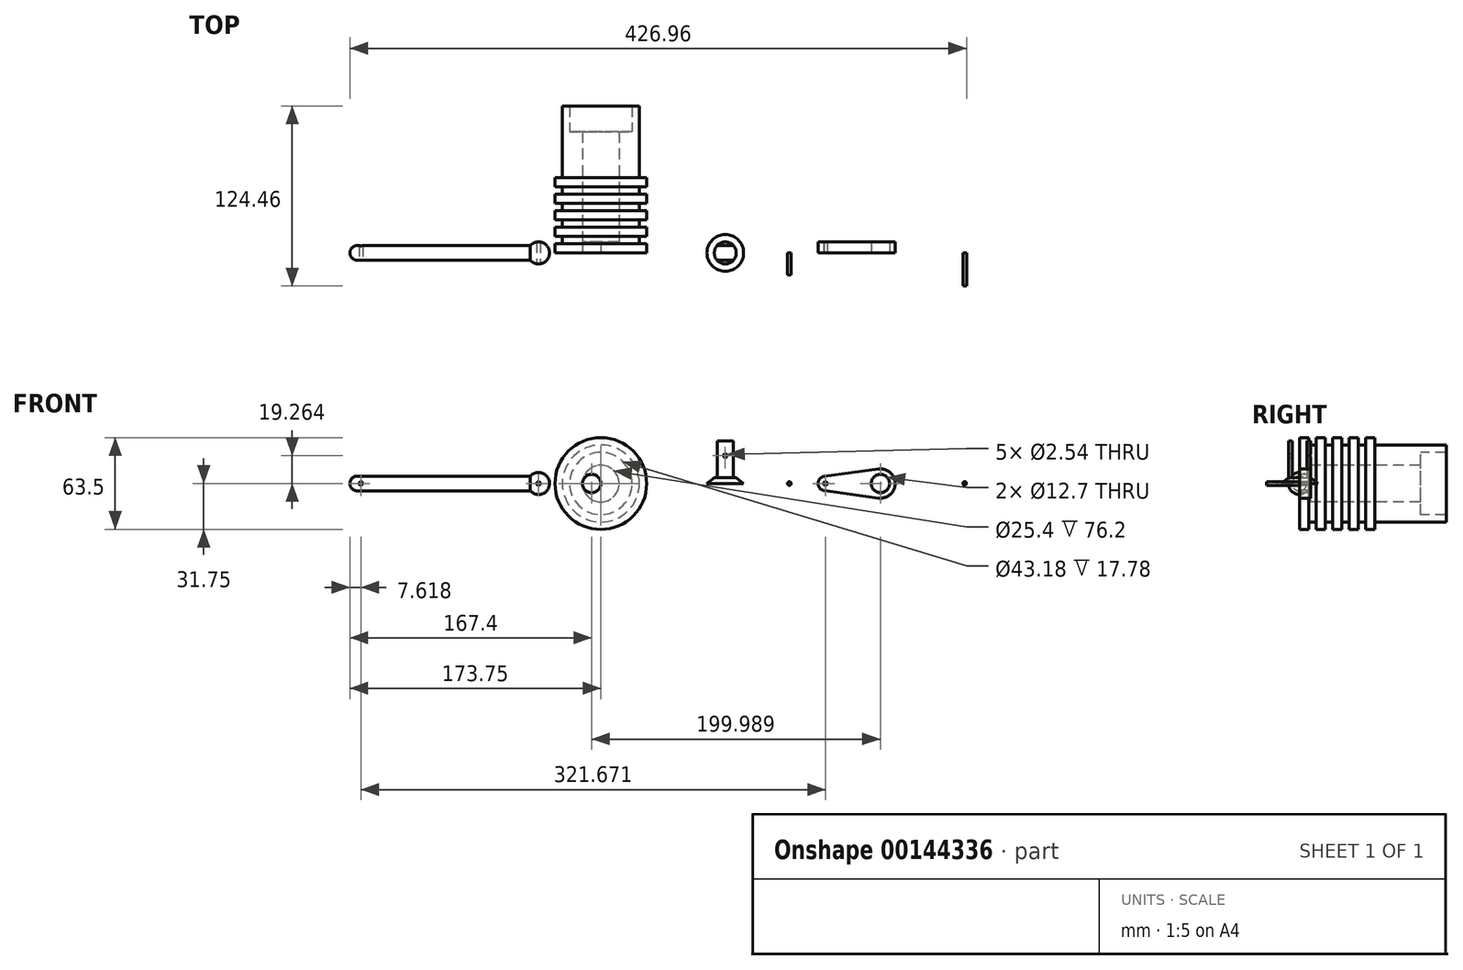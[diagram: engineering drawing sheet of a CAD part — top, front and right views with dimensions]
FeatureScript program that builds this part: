
annotation { "Feature Type Name" : "Feature", "Feature Type Description" : "" }
export const myFeature = defineFeature(function(context is Context, id is Id, definition is map)
    precondition{}
    {
        {
            var Q0;
            Q0=qCreatedBy(makeId("Top.planeOp"),FACE);
            var sketch = newSketch(context, id + "F0", { "sketchPlane" : qUnion([Q0])});
            skLineSegment(sketch, "E0", {"start": v(-31.75, 0) * mm, "end": v(-31.75, 6.35) * mm});
            skLineSegment(sketch, "E1", {"start": v(-31.75, 6.35) * mm, "end": v(-26.67, 6.35) * mm});
            skLineSegment(sketch, "E2", {"start": v(-26.67, 6.35) * mm, "end": v(-26.67, 11.43) * mm});
            skLineSegment(sketch, "E3", {"start": v(-26.67, 11.43) * mm, "end": v(-31.75, 11.43) * mm});
            skLineSegment(sketch, "E4", {"start": v(-31.75, 11.43) * mm, "end": v(-31.75, 17.78) * mm});
            skLineSegment(sketch, "E5", {"start": v(-31.75, 17.78) * mm, "end": v(-26.67, 17.78) * mm});
            skLineSegment(sketch, "E6", {"start": v(-26.67, 17.78) * mm, "end": v(-26.67, 22.86) * mm});
            skLineSegment(sketch, "E7", {"start": v(-26.67, 22.86) * mm, "end": v(-31.75, 22.86) * mm});
            skLineSegment(sketch, "E8", {"start": v(-31.75, 22.86) * mm, "end": v(-31.75, 29.21) * mm});
            skLineSegment(sketch, "E9", {"start": v(-31.75, 29.21) * mm, "end": v(-26.67, 29.21) * mm});
            skLineSegment(sketch, "E10", {"start": v(-26.67, 29.21) * mm, "end": v(-26.67, 34.3) * mm});
            skLineSegment(sketch, "E11", {"start": v(-26.67, 34.3) * mm, "end": v(-31.75, 34.3) * mm});
            skLineSegment(sketch, "E12", {"start": v(-31.75, 34.3) * mm, "end": v(-31.75, 40.64) * mm});
            skLineSegment(sketch, "E13", {"start": v(-31.75, 40.64) * mm, "end": v(-26.67, 40.64) * mm});
            skLineSegment(sketch, "E14", {"start": v(-26.67, 40.64) * mm, "end": v(-26.67, 45.72) * mm});
            skLineSegment(sketch, "E15", {"start": v(-26.67, 45.72) * mm, "end": v(-31.75, 45.72) * mm});
            skLineSegment(sketch, "E16", {"start": v(-31.75, 45.72) * mm, "end": v(-31.75, 52.07) * mm});
            skLineSegment(sketch, "E17", {"start": v(-31.75, 52.07) * mm, "end": v(-26.67, 52.07) * mm});
            skLineSegment(sketch, "E18", {"start": v(-26.67, 52.07) * mm, "end": v(-26.67, 101.6) * mm});
            skLineSegment(sketch, "E19", {"start": v(-26.67, 101.6) * mm, "end": v(-21.6, 101.6) * mm});
            skLineSegment(sketch, "E20", {"start": v(-21.6, 101.6) * mm, "end": v(-21.6, 83.82) * mm});
            skLineSegment(sketch, "E21", {"start": v(-21.6, 83.82) * mm, "end": v(-12.7, 83.82) * mm});
            skLineSegment(sketch, "E22", {"start": v(-1.27, 7.62) * mm, "end": v(-12.7, 7.62) * mm});
            skLineSegment(sketch, "E23", {"start": v(-12.7, 7.62) * mm, "end": v(-12.7, 83.82) * mm});
            skLineSegment(sketch, "E24", {"start": v(-31.75, 0) * mm, "end": v(-1.27, 0) * mm});
            skLineSegment(sketch, "E25", {"start": v(-1.27, 0) * mm, "end": v(-1.27, 7.62) * mm});
            skLineSegment(sketch, "E26", {"start": v(0, 0) * mm, "end": v(0, 138.75) * mm, "construction": true});
            skSolve(sketch);
        }
        {
            var Q0;
            Q0 = qSketchRegion(id + "F0", true);
            var Q1;
            Q1=sQuery(id+"F0.wireOp",EDGE,"E26");
            revolve(context, id + "F1", {"entities" : qUnion([Q0]), "axis" : qUnion([Q1]), "revolveType" : RevolveType.FULL});
        }
        {
            var Q0;
            Q0=makeQuery(id+"F1.opRevolve","SWEPT_FACE",FACE,{"disambiguationData":[OSD([sQuery(id+"F0.wireOp",EDGE,"E24")])]});
            var sketch = newSketch(context, id + "F2", { "sketchPlane" : qUnion([Q0])});
            skCircle(sketch, "E27.0", {"center": v(0, 0) * mm, "radius": 1.27 * mm});
            skSolve(sketch);
        }
        {
            var Q0;
            Q0 = qSketchRegion(id + "F2", true);
            extrude(context, id + "F3", {"entities" : qUnion([Q0]), "operationType" : NewBodyOperationType.ADD, "oppositeDirection" : true, "depth" : 7.62 * mm});
        }
        {
            var Q0;
            Q0=qCreatedBy(makeId("Front.planeOp"),FACE);
            var sketch = newSketch(context, id + "F4", { "sketchPlane" : qUnion([Q0])});
            skLineSegment(sketch, "E28", {"start": v(86.19, 0) * mm, "end": v(86.19, 29.98) * mm, "construction": true});
            skLineSegment(sketch, "E29", {"start": v(73.49, 0) * mm, "end": v(78.57, 4.02) * mm});
            skLineSegment(sketch, "E30", {"start": v(78.57, 4.02) * mm, "end": v(86.19, 4.02) * mm});
            skLineSegment(sketch, "E31", {"start": v(86.19, 4.02) * mm, "end": v(86.19, 0) * mm});
            skLineSegment(sketch, "E32", {"start": v(73.49, 0) * mm, "end": v(86.19, 0) * mm});
            skSolve(sketch);
        }
        {
            var Q0;
            Q0 = qSketchRegion(id + "F4", true);
            var Q1;
            Q1=sQuery(id+"F4.wireOp",EDGE,"E28");
            revolve(context, id + "F5", {"entities" : qUnion([Q0]), "axis" : qUnion([Q1]), "revolveType" : RevolveType.FULL});
        }
        {
            var Q0;
            Q0=makeQuery(id+"F5.opRevolve","SWEPT_FACE",FACE,{"disambiguationData":[OSD([sQuery(id+"F4.wireOp",EDGE,"E30")])]});
            var sketch = newSketch(context, id + "F6", { "sketchPlane" : qUnion([Q0])});
            skLineSegment(sketch, "E33", {"start": v(80.5, 5.08) * mm, "end": v(91.87, 5.08) * mm});
            skLineSegment(sketch, "E34", {"start": v(80.5, -5.08) * mm, "end": v(91.87, -5.08) * mm});
            skSolve(sketch);
        }
        {
            var Q0;
            Q0 = qSketchRegion(id + "F6", true);
            var Q1;
            {var subQ0=sQuery(id+"F6.wireOp",EDGE,"E33");Q1=makeQuery(id+"F6.imprint","IMPRINT",FACE,{"disambiguationData":[TD([[makeQuery(id+"F6.imprint","IMPRINT",EDGE,{"derivedFrom":subQ0}),1.0]])]});}
            var Q2;
            {var subQ0=sQuery(id+"F6.wireOp",EDGE,"E34");Q2=makeQuery(id+"F6.imprint","IMPRINT",FACE,{"disambiguationData":[TD([[makeQuery(id+"F6.imprint","IMPRINT",EDGE,{"derivedFrom":subQ0}),-1.0]])]});}
            extrude(context, id + "F7", {"entities" : qUnion([Q0, Q1, Q2]), "operationType" : NewBodyOperationType.ADD, "depth" : 25.4 * mm});
        }
        {
            var Q0;
            Q0=makeQuery(id+"F7.opExtrude","SWEPT_FACE",FACE,{"disambiguationData":[OSD([sQuery(id+"F6.wireOp",EDGE,"E33")])]});
            var sketch = newSketch(context, id + "F8", { "sketchPlane" : qUnion([Q0])});
            skCircle(sketch, "E35", {"center": v(86.18, 19.26) * mm, "radius": 1.27 * mm});
            skSolve(sketch);
        }
        {
            var Q0;
            Q0 = qSketchRegion(id + "F8", true);
            extrude(context, id + "F9", {"entities" : qUnion([Q0]), "operationType" : NewBodyOperationType.REMOVE, "depth" : 25.4 * mm});
        }
        {
            var Q0;
            Q0=makeQuery(id+"F7.opExtrude","SWEPT_FACE",FACE,{"disambiguationData":[OSD([sQuery(id+"F6.wireOp",EDGE,"E34")])]});
            var sketch = newSketch(context, id + "F10", { "sketchPlane" : qUnion([Q0])});
            skCircle(sketch, "E36.0", {"center": v(-86.18, 19.26) * mm, "radius": 1.27 * mm});
            skSolve(sketch);
        }
        {
            var Q0;
            Q0 = qSketchRegion(id + "F10", true);
            extrude(context, id + "F11", {"entities" : qUnion([Q0]), "operationType" : NewBodyOperationType.REMOVE, "depth" : 25.4 * mm});
        }
        {
            var Q0;
            Q0=qCreatedBy(makeId("Front.planeOp"),FACE);
            var sketch = newSketch(context, id + "F12", { "sketchPlane" : qUnion([Q0])});
            skLineSegment(sketch, "E37", {"start": v(130.56, 0) * mm, "end": v(130.56, 58.67) * mm, "construction": true});
            skCircle(sketch, "E38", {"center": v(130.56, 0) * mm, "radius": 1.27 * mm});
            skSolve(sketch);
        }
        {
            var Q0;
            Q0 = qSketchRegion(id + "F12", true);
            extrude(context, id + "F13", {"entities" : qUnion([Q0]), "depth" : 15.24 * mm});
        }
        {
            var Q0;
            Q0=qCreatedBy(makeId("Front.planeOp"),FACE);
            var sketch = newSketch(context, id + "F14", { "sketchPlane" : qUnion([Q0])});
            skLineSegment(sketch, "E39", {"start": v(0, 0) * mm, "end": v(-188.23, 0) * mm, "construction": true});
            skLineSegment(sketch, "E40", {"start": v(-168.67, 5.08) * mm, "end": v(-48.82, 5.08) * mm});
            skArc(sketch, "E41", {"start": v(-168.67, 5.08) * mm, "mid": v(-172.26, 3.6) * mm, "end": v(-173.75, 0) * mm});
            skArc(sketch, "E42", {"start": v(-35.52, 0) * mm, "mid": v(-40.43, 7.12) * mm, "end": v(-48.82, 5.08) * mm});
            skLineSegment(sketch, "E43", {"start": v(-173.75, 0) * mm, "end": v(-35.52, 0) * mm});
            skCircle(sketch, "E44", {"center": v(-43.14, 0) * mm, "radius": 1.27 * mm});
            skSolve(sketch);
        }
        {
            var Q0;
            Q0 = qSketchRegion(id + "F14", true);
            var Q1;
            Q1=sQuery(id+"F14.wireOp",EDGE,"E39");
            revolve(context, id + "F15", {"entities" : qUnion([Q0]), "axis" : qUnion([Q1]), "revolveType" : RevolveType.FULL});
        }
        {
            var Q0;
            Q0=qCreatedBy(makeId("Front.planeOp"),FACE);
            var sketch = newSketch(context, id + "F16", { "sketchPlane" : qUnion([Q0])});
            skCircle(sketch, "E45", {"center": v(-166.13, 0) * mm, "radius": 1.27 * mm});
            skSolve(sketch);
        }
        {
            var Q0;
            Q0 = qSketchRegion(id + "F16", true);
            extrude(context, id + "F17", {"entities" : qUnion([Q0]), "operationType" : NewBodyOperationType.REMOVE, "oppositeDirection" : true, "depth" : 25.4 * mm});
        }
        {
            var Q0;
            Q0=qCreatedBy(makeId("Front.planeOp"),FACE);
            var sketch = newSketch(context, id + "F18", { "sketchPlane" : qUnion([Q0])});
            skCircle(sketch, "E46.0", {"center": v(-166.13, 0) * mm, "radius": 1.27 * mm});
            skSolve(sketch);
        }
        {
            var Q0;
            Q0 = qSketchRegion(id + "F18", true);
            extrude(context, id + "F19", {"entities" : qUnion([Q0]), "operationType" : NewBodyOperationType.REMOVE, "depth" : 25.4 * mm});
        }
        {
            var Q0;
            Q0=makeQuery(id+"F3.boolean.opBoolean","MERGE",FACE,{"derivedFrom":[makeQuery(id+"F1.opRevolve","SWEPT_FACE",FACE,{"disambiguationData":[OSD([sQuery(id+"F0.wireOp",EDGE,"E24")])]}),makeQuery(id+"F3.opExtrude","CAP_FACE",FACE,{"disambiguationData":[OSD([sQuery(id+"F2.wireOp",EDGE,"E27.0")])],"isStart":true})]});
            var sketch = newSketch(context, id + "F20", { "sketchPlane" : qUnion([Q0])});
            skCircle(sketch, "E47", {"center": v(-6.35, 0) * mm, "radius": 6.35 * mm});
            skSolve(sketch);
        }
        {
            var Q0;
            Q0 = qSketchRegion(id + "F20", true);
            extrude(context, id + "F21", {"entities" : qUnion([Q0]), "operationType" : NewBodyOperationType.REMOVE, "oppositeDirection" : true, "depth" : 25.4 * mm});
        }
        {
            var Q0;
            Q0=qCreatedBy(makeId("Front.planeOp"),FACE);
            var sketch = newSketch(context, id + "F22", { "sketchPlane" : qUnion([Q0])});
            skLineSegment(sketch, "E48", {"start": v(155.54, 0) * mm, "end": v(193.64, 0) * mm, "construction": true});
            skLineSegment(sketch, "E49", {"start": v(154.86, 5.03) * mm, "end": v(192.28, 10.07) * mm});
            skLineSegment(sketch, "E50", {"start": v(154.53, -4.98) * mm, "end": v(192.28, -10.07) * mm});
            skArc(sketch, "E51", {"start": v(154.86, 5.03) * mm, "mid": v(150.46, 0.17) * mm, "end": v(154.53, -4.98) * mm});
            skArc(sketch, "E52", {"start": v(192.28, 10.07) * mm, "mid": v(203.8, 0) * mm, "end": v(192.28, -10.07) * mm});
            skCircle(sketch, "E53", {"center": v(193.64, 0) * mm, "radius": 6.35 * mm});
            skCircle(sketch, "E54", {"center": v(155.54, 0) * mm, "radius": 1.27 * mm});
            skSolve(sketch);
        }
        {
            var Q0;
            Q0 = qSketchRegion(id + "F22", true);
            extrude(context, id + "F23", {"entities" : qUnion([Q0]), "oppositeDirection" : true, "depth" : 7.62 * mm});
        }
        {
            var Q0;
            Q0=qCreatedBy(makeId("Front.planeOp"),FACE);
            var sketch = newSketch(context, id + "F24", { "sketchPlane" : qUnion([Q0])});
            skCircle(sketch, "E55.0", {"center": v(-43.14, 0) * mm, "radius": 1.27 * mm});
            skSolve(sketch);
        }
        {
            var Q0;
            Q0 = qSketchRegion(id + "F24", true);
            var Q1;
            Q1=sQuery(id+"F24.wireOp",EDGE,"E55.0");
            extrude(context, id + "F25", {"entities" : qUnion([Q0]), "operationType" : NewBodyOperationType.REMOVE, "surfaceEntities" : qUnion([Q1]), "oppositeDirection" : true, "depth" : 25.4 * mm});
        }
        {
            var Q0;
            Q0=qCreatedBy(makeId("Front.planeOp"),FACE);
            var sketch = newSketch(context, id + "F26", { "sketchPlane" : qUnion([Q0])});
            skCircle(sketch, "E56.0", {"center": v(-43.14, 0) * mm, "radius": 1.27 * mm});
            skSolve(sketch);
        }
        {
            var Q0;
            Q0 = qSketchRegion(id + "F26", true);
            extrude(context, id + "F27", {"entities" : qUnion([Q0]), "operationType" : NewBodyOperationType.REMOVE, "depth" : 25.4 * mm});
        }
        {
            var Q0;
            Q0=qCreatedBy(makeId("Front.planeOp"),FACE);
            var sketch = newSketch(context, id + "F28", { "sketchPlane" : qUnion([Q0])});
            skLineSegment(sketch, "E57", {"start": v(251.94, 0) * mm, "end": v(251.94, 64.96) * mm, "construction": true});
            skCircle(sketch, "E58", {"center": v(251.94, 0) * mm, "radius": 1.27 * mm});
            skSolve(sketch);
        }
        {
            var Q0;
            Q0 = qSketchRegion(id + "F28", true);
            extrude(context, id + "F29", {"entities" : qUnion([Q0]), "depth" : 22.86 * mm});
        }
    });
